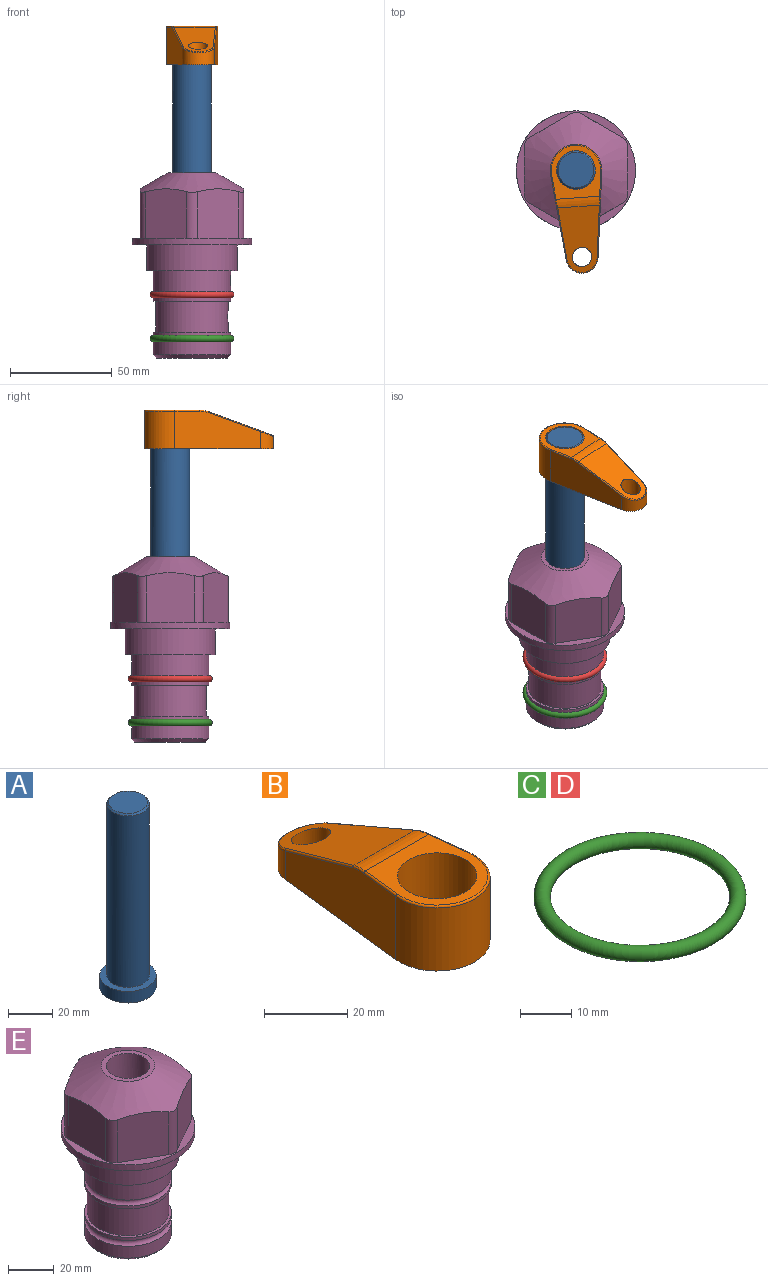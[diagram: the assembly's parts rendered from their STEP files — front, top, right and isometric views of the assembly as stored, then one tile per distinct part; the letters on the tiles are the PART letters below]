
ASSEMBLY  parts=5 mates=3
PART A: 6 faces, bbox 25.4x25.4x101.6 mm
  f0: plane 17.46x17.46mm, normal (0,0,1), area 239.5mm2, adj f5
  f1: plane 25.4x25.4mm, normal (0,0,-1), area 506.7mm2, adj f2
  f2: cylinder r=12.7mm len=25.4mm, axis (0,0,1), area 506.7mm2, adj f1,f3
  f3: plane 25.4x25.4mm, normal (0,0,1), area 221.7mm2, adj f2,f4
  f4: cylinder r=9.53mm len=94.46mm, axis (0,0,1), area 5653mm2, adj f3,f5
  f5: cone r=8.73mm half-angle=45deg, axis (0,0,-1), area 64.4mm2, adj f0,f4
PART B: 44 faces, bbox 27.5x64.5x19.1 mm
  f0: plane 2.3x0.95mm, normal (0,0,-1), area 1mm2, adj f25,f30,f34
  f1: plane 63.5x25.4mm, normal (0,0,-1), area 561.7mm2, adj f2,f3,f4,f5,f6,f7,f19,f20
  f2: cylinder r=12.7mm len=25.4mm, axis (0,0,-1), area 792.2mm2, adj f1,f3,f5,f13
  f3: plane 42.33x18.54mm, normal (0.99,0.11,0), area 647mm2, adj f1,f2,f4,f11,f12,f14
  f4: cylinder r=7.94mm len=15.78mm, axis (0,0,-1), area 158.6mm2, adj f1,f3,f5,f16
  f5: plane 42.33x18.54mm, normal (-0.99,0.11,0), area 647mm2, adj f1,f2,f4,f15,f17,f18
  f6: cylinder r=9.53mm len=19.05mm, axis (0,0,-1), area 1140.1mm2, adj f1,f8
  f7: cylinder r=4.76mm len=10.98mm, axis (0,0,-1), area 276.1mm2, adj f1,f9
  f8: plane 25.83x24.38mm, normal (0,0,1), area 262.2mm2, adj f6,f10,f11,f13,f15
  f9: plane 32.49x20.55mm, normal (0,0.34,0.94), area 489.9mm2, adj f7,f10,f14,f16,f18
  f10: cylinder r=12.7mm len=21.49mm, axis (-1,0,0), area 93.2mm2, adj f8,f9,f12,f17
  f11: cylinder r=0.51mm len=12.34mm, axis (0.11,-0.99,0), area 9.9mm2, adj f3,f8,f12,f13
  f12: bspline ~7.62x1.64mm, area 3.5mm2, adj f3,f10,f11,f14
  f13: torus R=12.19mm, axis (0,0,1), area 33.6mm2, adj f2,f8,f11,f15
  f14: cylinder r=0.51mm len=26.01mm, axis (0.1,-0.93,0.34), area 21.6mm2, adj f3,f9,f12,f16
  f15: cylinder r=0.51mm len=12.34mm, axis (0.11,0.99,0), area 9.9mm2, adj f5,f8,f13,f17
  f16: bspline ~15.78x7.05mm, area 15.7mm2, adj f4,f9,f14,f18
  f17: bspline ~7.62x1.64mm, area 3.5mm2, adj f5,f10,f15,f18
  f18: cylinder r=0.51mm len=26.01mm, axis (0.1,0.93,-0.34), area 21.6mm2, adj f5,f9,f16,f17
  f19: plane 21.6x14.29mm, normal (-0.99,-0.11,0), area 242.6mm2, adj f1,f26,f28,f34,f36,f38
  f20: plane 21.6x14.29mm, normal (0.99,-0.11,0), area 242.6mm2, adj f1,f27,f29,f37,f39,f41
  f21: cylinder r=12.7mm len=14.29mm, axis (0,0,-1), area 173.2mm2, adj f1,f26,f27,f30,f31,f33
  f22: cylinder r=7.94mm len=7.63mm, axis (0,0,-1), area 53.8mm2, adj f1,f28,f29,f42
  f23: plane 2.3x0.95mm, normal (0,0,-1), area 1mm2, adj f25,f33,f37
  f24: plane 17.94x12.32mm, normal (0,-0.34,-0.94), area 191.2mm2, adj f25,f38,f41,f42
  f25: cylinder r=9.53mm len=12.93mm, axis (-1,0,0), area 37.5mm2, adj f0,f23,f24,f31,f36,f39
  f26: cylinder r=1.59mm len=14.29mm, axis (0,0,-1), area 49mm2, adj f1,f19,f21,f32
  f27: cylinder r=1.59mm len=14.29mm, axis (0,0,-1), area 49mm2, adj f1,f20,f21,f35
  f28: cylinder r=1.59mm len=7.28mm, axis (0,0,-1), area 22.1mm2, adj f1,f19,f22,f40
  f29: cylinder r=1.59mm len=7.28mm, axis (0,0,-1), area 22.1mm2, adj f1,f20,f22,f43
  f30: torus R=14.29mm, axis (0,0,1), area 5.8mm2, adj f0,f21,f31,f32
  f31: bspline ~11.06x2.73mm, area 20.8mm2, adj f21,f25,f30,f33
  f32: sphere r=1.59mm, area 5.4mm2, adj f26,f30,f34
  f33: torus R=14.29mm, axis (0,0,1), area 5.8mm2, adj f21,f23,f31,f35
  f34: cylinder r=1.59mm len=1.68mm, axis (-0.11,0.99,0), area 2.4mm2, adj f0,f19,f32,f36
  f35: sphere r=1.59mm, area 5.4mm2, adj f27,f33,f37
  f36: bspline ~5.82x2.33mm, area 7.7mm2, adj f19,f25,f34,f38
  f37: cylinder r=1.59mm len=1.68mm, axis (0.11,0.99,0), area 2.4mm2, adj f20,f23,f35,f39
  f38: cylinder r=1.59mm len=18.33mm, axis (0.1,-0.93,0.34), area 46.7mm2, adj f19,f24,f36,f40
  f39: bspline ~5.82x2.33mm, area 7.7mm2, adj f20,f25,f37,f41
  f40: sphere r=1.59mm, area 3.6mm2, adj f28,f38,f42
  f41: cylinder r=1.59mm len=18.33mm, axis (0.1,0.93,-0.34), area 46.7mm2, adj f20,f24,f39,f43
  f42: bspline ~8.31x1.84mm, area 15.3mm2, adj f22,f24,f40,f43
  f43: sphere r=1.59mm, area 3.6mm2, adj f29,f41,f42
PART C: 1 faces, bbox 44.7x44.7x3.2 mm
  f0: torus R=19.05mm, axis (0,0,1), area 1193.9mm2
PART D: same geometry as C
PART E: 36 faces, bbox 58.7x58.7x91.2 mm
  f0: cylinder r=17.78mm len=35.56mm, axis (0,0,1), area 1670.8mm2, adj f23,f24,f31
  f1: cylinder r=19.05mm len=38.1mm, axis (0,0,1), area 1191.9mm2, adj f26,f27,f30
  f2: plane 58.66x58.66mm, normal (0,0,-1), area 1150.6mm2, adj f3,f28
  f3: cylinder r=29.33mm len=58.66mm, axis (0,0,-1), area 585.1mm2, adj f2,f4
  f4: plane 58.66x58.66mm, normal (0,0,1), area 475.9mm2, adj f3,f5,f6,f7,f8,f9,f10,f11
  f5: plane 24.5x20.32mm, normal (-0.5,0.87,0), area 562.8mm2, adj f4,f15,f16,f17
  f6: plane 24.5x20.32mm, normal (0.5,0.87,0), area 562.8mm2, adj f4,f14,f15,f17
  f7: plane 24.5x23.48mm, normal (1,0,0), area 562.8mm2, adj f4,f13,f14,f17
  f8: plane 24.5x20.32mm, normal (0.5,-0.87,0), area 562.8mm2, adj f4,f12,f13,f17
  f9: plane 24.5x20.32mm, normal (-0.5,-0.87,0), area 562.8mm2, adj f4,f11,f12,f17
  f10: plane 24.5x23.48mm, normal (-1,0,0), area 562.8mm2, adj f4,f11,f16,f17
  f11: cylinder r=5.08mm len=23.01mm, axis (0,0,-1), area 121.2mm2, adj f4,f9,f10,f17
  f12: cylinder r=5.08mm len=23.01mm, axis (0,0,-1), area 121.2mm2, adj f4,f8,f9,f17
  f13: cylinder r=5.08mm len=23.01mm, axis (0,0,-1), area 121.2mm2, adj f4,f7,f8,f17
  f14: cylinder r=5.08mm len=23.01mm, axis (0,0,-1), area 121.2mm2, adj f4,f6,f7,f17
  f15: cylinder r=5.08mm len=23.01mm, axis (0,0,-1), area 121.2mm2, adj f4,f5,f6,f17
  f16: cylinder r=5.08mm len=23.01mm, axis (0,0,-1), area 121.2mm2, adj f4,f5,f10,f17
  f17: cone r=11.73mm half-angle=60deg, axis (0,0,-1), area 2071.8mm2, adj f5,f6,f7,f8,f9,f10,f11,f12
  f18: plane 23.46x23.46mm, normal (0,0,1), area 147.4mm2, adj f17,f35
  f19: plane 34.93x34.93mm, normal (0,0,-1), area 958mm2, adj f29
  f20: cylinder r=19.05mm len=38.1mm, axis (0,0,1), area 760.1mm2, adj f21,f29
  f21: torus R=19.05mm, axis (0,0,1), area 565.3mm2, adj f20,f22
  f22: cylinder r=19.05mm len=38.1mm, axis (0,0,1), area 190mm2, adj f21,f23
  f23: plane 38.1x38.1mm, normal (0,0,1), area 146.9mm2, adj f0,f22
  f24: plane 38.1x38.1mm, normal (0,0,-1), area 146.9mm2, adj f0,f25
  f25: cylinder r=19.05mm len=38.1mm, axis (0,0,1), area 190mm2, adj f24,f26
  f26: torus R=19.05mm, axis (0,0,1), area 565.3mm2, adj f1,f25
  f27: plane 44.45x44.45mm, normal (0,0,-1), area 411.7mm2, adj f1,f28
  f28: cylinder r=22.23mm len=44.45mm, axis (0,0,1), area 1773.5mm2, adj f2,f27
  f29: cone r=19.05mm half-angle=45deg, axis (0,0,1), area 257.5mm2, adj f19,f20
  f30: cylinder r=3.17mm len=6.75mm, axis (-1,0,0), area 128mm2, adj f1,f33
  f31: cylinder r=3.17mm len=6.35mm, axis (-1,0,0), area 102.5mm2, adj f0,f33
  f32: plane 25.4x25.4mm, normal (0,0,1), area 506.7mm2, adj f33
  f33: cylinder r=12.7mm len=66.42mm, axis (0,0,-1), area 5236.2mm2, adj f30,f31,f32,f34
  f34: cone r=9.53mm half-angle=30deg, axis (0,0,-1), area 443.4mm2, adj f33,f35
  f35: cylinder r=9.53mm len=19.05mm, axis (0,0,-1), area 849mm2, adj f18,f34
PLACE A rot(axis=(0,0,-1),86.1deg) t=(0,0,34.07)mm
PLACE B rot(axis=(0,0,-1),176.1deg) t=(0,0,88.68)mm
PLACE C t=(0,0,-21.59)mm
PLACE D at identity
PLACE E at identity fixed
MATE fastened C.f0 <-> E.f0  axis (0,0,1) through (0,0,-46.1)mm
MATE cylindrical A.f2 <-> E.f0  axis (0,0,1) through (0,0,59.7)mm
MATE fastened B.f2 <-> A.f2  axis (0,0,1) through (0,0,107.73)mm
